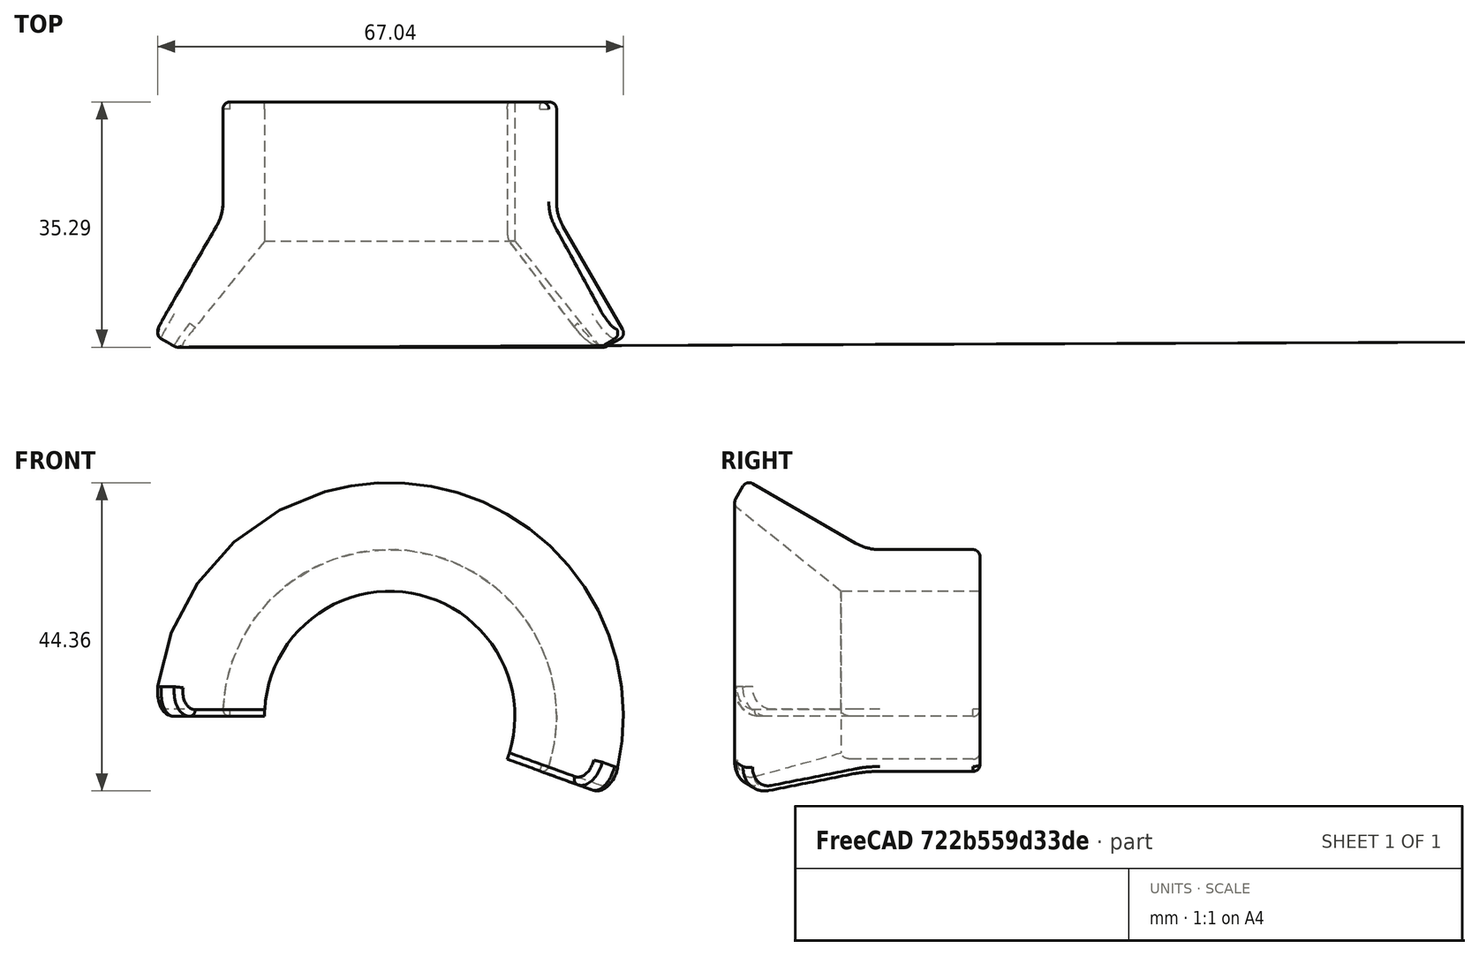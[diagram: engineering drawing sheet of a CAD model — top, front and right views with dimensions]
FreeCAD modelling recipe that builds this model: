
FCSTD DOCUMENT  (FreeCAD 0.16R)
Label: HoseDeflector
License: All rights reserved
LicenseURL: http://en.wikipedia.org/wiki/All_rights_reserved
objects: PartDesign::Fillet×5, Sketcher::SketchObject×1, PartDesign::Revolution×1, Mesh::Feature×1
note: 8 computed .brp shape members not serialized (recipe doc carries the construction recipe); baked Part::Feature solids carry a one-line shape summary decoded from their .brp

FEATURE [Sketcher::SketchObject] Sketch
  sketch-geometry (6):
    g0: LineSegment StartX=-24 StartY=27.5776 StartZ=0 EndX=-18 EndY=27.5776 EndZ=0
    g1: LineSegment StartX=-18 StartY=27.5776 StartZ=0 EndX=-18 EndY=7.57764 EndZ=0
    g2: LineSegment StartX=-24 StartY=27.5776 StartZ=0 EndX=-24 EndY=11.3145 EndZ=0
    g3: LineSegment StartX=-24 StartY=11.3145 StartZ=0 EndX=-34 EndY=-6.00604 EndZ=0
    g4: LineSegment StartX=-34 StartY=-6.00604 StartZ=0 EndX=-30.5359 EndY=-8.00604 EndZ=0
    g5: LineSegment StartX=-30.5359 StartY=-8.00604 StartZ=0 EndX=-18 EndY=7.57764 EndZ=0
  constraints (17):
    c: Horizontal(g0)
    c: Coincident(g0,g1)
    c: Vertical(g1)
    c: Coincident(g0,g2)
    c: Vertical(g2)
    c: Coincident(g2,g3)
    c: Coincident(g3,g4)
    c: Coincident(g4,g5)
    c: Coincident(g5,g1)
    c: Equal(g5,g3)
    c: Perpendicular(g3,g4)
    c: Distance(g4) = 4
    c: Distance(g0) = 6
    c: DistanceX(g0) = -18
    c: Distance(g1) = 20
    c: Angle(g2,g3) = 2.61799
    c: Distance(g3) = 20
FEATURE [PartDesign::Revolution] Revolution
  Angle = 200
  Axis = (0,1,0)
  Base = (0,0,0)
  ReferenceAxis = -> Sketch [V_Axis]
  Sketch = -> Sketch
FEATURE [PartDesign::Fillet] Fillet
  Base = -> Revolution [Edge13,Edge12]
  Radius = 4
FEATURE [PartDesign::Fillet] Fillet001
  Base = -> Fillet [Edge23]
  Radius = 7
FEATURE [PartDesign::Fillet] Fillet002
  Base = -> Fillet001 [Edge17]
  Radius = 1
FEATURE [PartDesign::Fillet] Fillet003
  Base = -> Fillet002 [Edge20]
  Radius = 1
FEATURE [PartDesign::Fillet] Fillet004
  Base = -> Fillet003 [Edge15]
  Radius = 1
FEATURE [Mesh::Feature] Mesh  label="Fillet004 (Meshed)"
